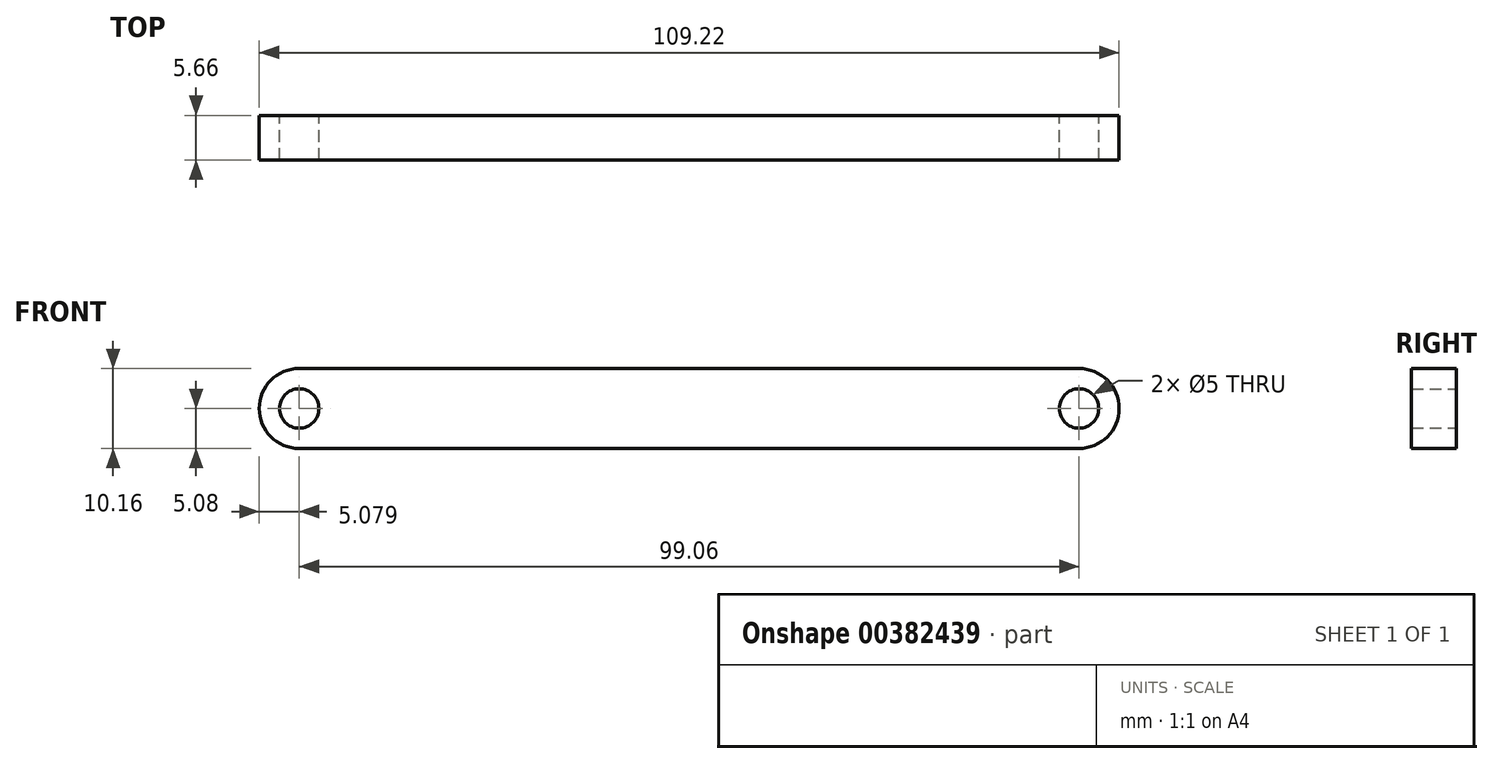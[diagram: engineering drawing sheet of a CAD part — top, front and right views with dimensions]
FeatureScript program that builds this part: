
annotation { "Feature Type Name" : "Feature", "Feature Type Description" : "" }
export const myFeature = defineFeature(function(context is Context, id is Id, definition is map)
    precondition{}
    {
        {
            var Q0;
            Q0=qCreatedBy(makeId("Front.planeOp"),FACE);
            var sketch = newSketch(context, id + "F0", { "sketchPlane" : qUnion([Q0])});
            skArc(sketch, "E0", {"start": v(-63.52, 5.08) * mm, "mid": v(-68.6, 0) * mm, "end": v(-63.52, -5.08) * mm});
            skArc(sketch, "E1", {"start": v(35.54, -5.08) * mm, "mid": v(40.62, 0) * mm, "end": v(35.54, 5.08) * mm});
            skLineSegment(sketch, "E2", {"start": v(-63.52, 5.08) * mm, "end": v(35.54, 5.08) * mm});
            skLineSegment(sketch, "E3", {"start": v(-63.52, -5.08) * mm, "end": v(35.54, -5.08) * mm});
            skCircle(sketch, "E4", {"center": v(-63.52, 0) * mm, "radius": 2.5 * mm});
            skCircle(sketch, "E5", {"center": v(35.54, 0) * mm, "radius": 2.5 * mm});
            skSolve(sketch);
        }
        {
            var Q0;
            Q0=makeQuery(id+"F0.imprint","IMPRINT",FACE,{"disambiguationData":[TD([[makeQuery(id+"F0.imprint","IMPRINT",EDGE,{"derivedFrom":sQuery(id+"F0.wireOp",EDGE,"E0")}),1.0]])]});
            extrude(context, id + "F1", {"entities" : qUnion([Q0]), "depth" : 5.66 * mm});
        }
    });
